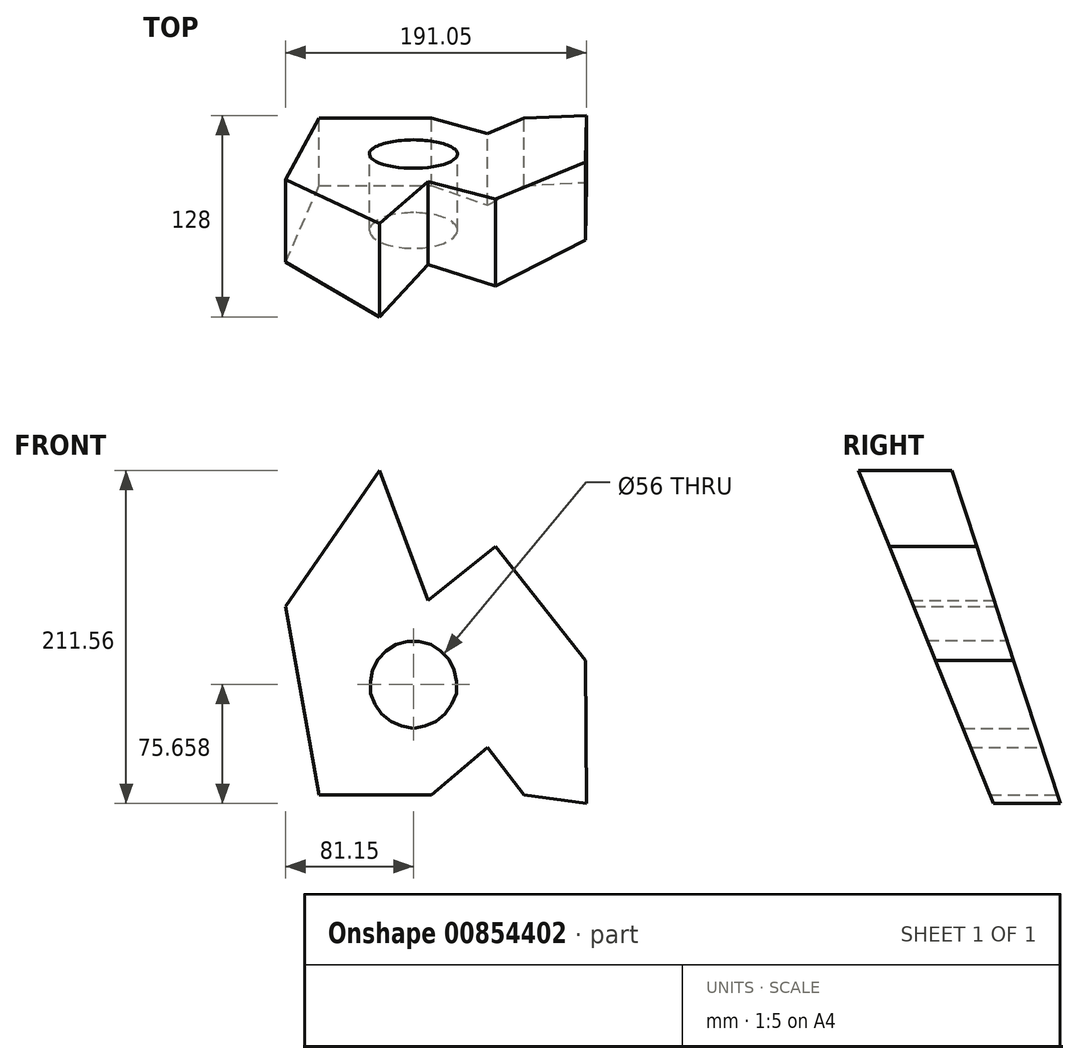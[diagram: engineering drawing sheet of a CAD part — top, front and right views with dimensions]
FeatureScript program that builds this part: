
annotation { "Feature Type Name" : "Feature", "Feature Type Description" : "" }
export const myFeature = defineFeature(function(context is Context, id is Id, definition is map)
    precondition{}
    {
        {
            var Q0;
            Q0=qCreatedBy(makeId("Front.planeOp"),FACE);
            var sketch = newSketch(context, id + "F0", { "sketchPlane" : qUnion([Q0])});
            skLineSegment(sketch, "E0", {"start": v(-21.43, 120.56) * mm, "end": v(-81.15, 34.2) * mm});
            skLineSegment(sketch, "E1", {"start": v(-21.43, 120.56) * mm, "end": v(9.15, 38.05) * mm});
            skLineSegment(sketch, "E2", {"start": v(9.15, 38.05) * mm, "end": v(52.3, 72.16) * mm});
            skLineSegment(sketch, "E3", {"start": v(52.3, 72.16) * mm, "end": v(109.36, 0) * mm});
            skLineSegment(sketch, "E4", {"start": v(109.36, 0) * mm, "end": v(109.9, -91) * mm});
            skLineSegment(sketch, "E5", {"start": v(109.9, -91) * mm, "end": v(70.25, -85.66) * mm});
            skLineSegment(sketch, "E6", {"start": v(70.25, -85.66) * mm, "end": v(47.2, -55.46) * mm});
            skLineSegment(sketch, "E7", {"start": v(47.2, -119.83) * mm, "end": v(-59.8, -119.83) * mm});
            skLineSegment(sketch, "E8", {"start": v(47.2, -55.46) * mm, "end": v(-5.77, -100.48) * mm});
            skLineSegment(sketch, "E9", {"start": v(11.65, -85.66) * mm, "end": v(-59.8, -85.66) * mm});
            skLineSegment(sketch, "E10", {"start": v(-59.8, -85.66) * mm, "end": v(-81.15, 34.2) * mm});
            skCircle(sketch, "E11", {"center": v(0, -15.34) * mm, "radius": 28 * mm});
            skSolve(sketch);
        }
        {
            var Q0;
            Q0=makeQuery(id+"F0.imprint","IMPRINT",FACE,{"disambiguationData":[TD([[makeQuery(id+"F0.imprint","IMPRINT",EDGE,{"derivedFrom":sQuery(id+"F0.wireOp",EDGE,"E0")}),1.0]])]});
            extrude(context, id + "F1", {"entities" : qUnion([Q0]), "depth" : 300 * mm, "offsetDistance" : 25 * mm});
        }
        {
            var Q0;
            Q0=qCreatedBy(makeId("Right.planeOp"),FACE);
            var sketch = newSketch(context, id + "F2", { "sketchPlane" : qUnion([Q0])});
            skLineSegment(sketch, "E12.0.0", {"start": v(0, -91) * mm, "end": v(0, 0) * mm});
            skLineSegment(sketch, "E12.0.1", {"start": v(0, 0) * mm, "end": v(-300, 0) * mm});
            skLineSegment(sketch, "E12.0.2", {"start": v(-300, 0) * mm, "end": v(-300, -91) * mm});
            skLineSegment(sketch, "E12.0.3", {"start": v(-300, -91) * mm, "end": v(0, -91) * mm});
            skLineSegment(sketch, "E13", {"start": v(0, -91) * mm, "end": v(-128, -91) * mm});
            skLineSegment(sketch, "E14", {"start": v(0, -91) * mm, "end": v(102.42, -91) * mm});
            skLineSegment(sketch, "E15", {"start": v(0, -91) * mm, "end": v(-74.41, 138.03) * mm});
            skLineSegment(sketch, "E16.0.0", {"start": v(0, 38.05) * mm, "end": v(0, 120.56) * mm});
            skLineSegment(sketch, "E16.0.1", {"start": v(0, 120.56) * mm, "end": v(-300, 120.56) * mm});
            skLineSegment(sketch, "E16.0.2", {"start": v(-300, 120.56) * mm, "end": v(-300, 38.05) * mm});
            skLineSegment(sketch, "E16.0.3", {"start": v(-300, 38.05) * mm, "end": v(0, 38.05) * mm});
            skLineSegment(sketch, "E17", {"start": v(-128, -91) * mm, "end": v(-128, 120.56) * mm});
            skLineSegment(sketch, "E18", {"start": v(-128, 120.56) * mm, "end": v(-20.16, -146.35) * mm});
            skLineSegment(sketch, "E19", {"start": v(-300, 38.05) * mm, "end": v(-300, 0) * mm});
            skLineSegment(sketch, "E20", {"start": v(0, 38.05) * mm, "end": v(0, 0) * mm});
            skSolve(sketch);
        }
        {
            var Q0;
            {var subQ3=sQuery(id+"F2.wireOp",EDGE,"E16.0.2");Q0=makeQuery(id+"F2.imprint","IMPRINT",FACE,{"disambiguationData":[TD([[makeQuery(id+"F2.imprint","IMPRINT",EDGE,{"derivedFrom":subQ3}),1.0]])]});}
            var Q1;
            {var subQ0=sQuery(id+"F2.wireOp",EDGE,"E18");var subQ1=sQuery(id+"F2.wireOp",EDGE,"E16.0.3");var subQ2=makeQuery(id+"F2.imprint","INTERSECT",VERTEX,{"derivedFrom":[subQ1,subQ0]});Q1=makeQuery(id+"F2.imprint","IMPRINT",FACE,{"disambiguationData":[TD([[makeQuery(id+"F2.imprint","IMPRINT",EDGE,{"disambiguationData":[TD([[subQ2,1.0]])],"derivedFrom":subQ1}),1.0]])]});}
            var Q2;
            {var subQ3=sQuery(id+"F2.wireOp",EDGE,"E19");Q2=makeQuery(id+"F2.imprint","IMPRINT",FACE,{"disambiguationData":[TD([[makeQuery(id+"F2.imprint","IMPRINT",EDGE,{"derivedFrom":subQ3}),1.0]])]});}
            var Q3;
            {var subQ0=sQuery(id+"F2.wireOp",EDGE,"E17");var subQ1=sQuery(id+"F2.wireOp",EDGE,"E12.0.1");var subQ2=makeQuery(id+"F2.imprint","INTERSECT",VERTEX,{"derivedFrom":[subQ1,subQ0]});Q3=makeQuery(id+"F2.imprint","IMPRINT",FACE,{"disambiguationData":[TD([[makeQuery(id+"F2.imprint","IMPRINT",EDGE,{"disambiguationData":[TD([[subQ2,1.0]])],"derivedFrom":subQ1}),-1.0]])]});}
            var Q4;
            {var subQ3=sQuery(id+"F2.wireOp",EDGE,"E12.0.2");Q4=makeQuery(id+"F2.imprint","IMPRINT",FACE,{"disambiguationData":[TD([[makeQuery(id+"F2.imprint","IMPRINT",EDGE,{"derivedFrom":subQ3}),1.0]])]});}
            var Q5;
            {var subQ0=sQuery(id+"F2.wireOp",EDGE,"E17");var subQ1=sQuery(id+"F2.wireOp",EDGE,"E12.0.1");var subQ2=makeQuery(id+"F2.imprint","INTERSECT",VERTEX,{"derivedFrom":[subQ1,subQ0]});Q5=makeQuery(id+"F2.imprint","IMPRINT",FACE,{"disambiguationData":[TD([[makeQuery(id+"F2.imprint","IMPRINT",EDGE,{"disambiguationData":[TD([[subQ2,1.0]])],"derivedFrom":subQ1}),1.0]])]});}
            var Q6;
            {var subQ5=sQuery(id+"F2.wireOp",EDGE,"E16.0.0");Q6=makeQuery(id+"F2.imprint","IMPRINT",FACE,{"disambiguationData":[TD([[makeQuery(id+"F2.imprint","IMPRINT",EDGE,{"derivedFrom":subQ5}),1.0]])]});}
            var Q7;
            {var subQ0=sQuery(id+"F2.wireOp",EDGE,"E20");Q7=makeQuery(id+"F2.imprint","IMPRINT",FACE,{"disambiguationData":[TD([[makeQuery(id+"F2.imprint","IMPRINT",EDGE,{"derivedFrom":subQ0}),-1.0]])]});}
            var Q8;
            {var subQ0=sQuery(id+"F2.wireOp",EDGE,"E12.0.0");Q8=makeQuery(id+"F2.imprint","IMPRINT",FACE,{"disambiguationData":[TD([[makeQuery(id+"F2.imprint","IMPRINT",EDGE,{"derivedFrom":subQ0}),1.0]])]});}
            extrude(context, id + "F3", {"entities" : qUnion([Q0, Q1, Q2, Q3, Q4, Q5, Q6, Q7, Q8]), "operationType" : NewBodyOperationType.REMOVE, "depth" : 451 * mm, "offsetDistance" : 25 * mm, "hasSecondDirection" : true, "secondDirectionOppositeDirection" : true, "secondDirectionDepth" : 227 * mm});
        }
    });
